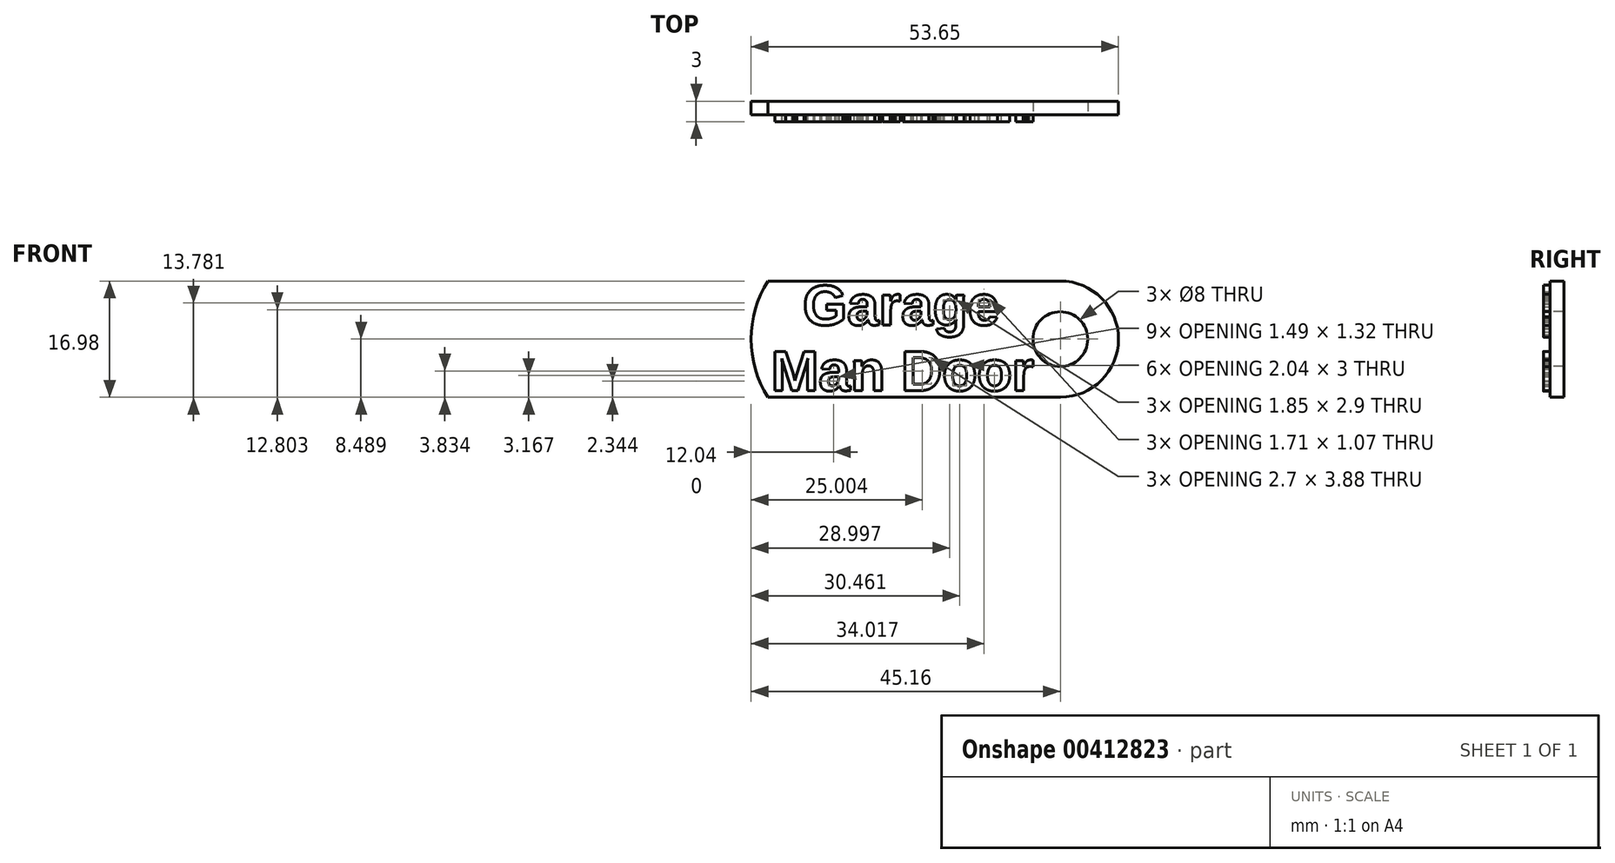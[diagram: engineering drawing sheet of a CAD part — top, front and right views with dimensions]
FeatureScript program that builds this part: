
annotation { "Feature Type Name" : "Feature", "Feature Type Description" : "" }
export const myFeature = defineFeature(function(context is Context, id is Id, definition is map)
    precondition{}
    {
        {
            var Q0;
            Q0=qCreatedBy(makeId("Front.planeOp"),FACE);
            var sketch = newSketch(context, id + "F0", { "sketchPlane" : qUnion([Q0])});
            skText(sketch, "E0", { "text": "   Garage \n Man Door\n", "fontName": "Arimo-Bold.ttf"});
            const initialGuessF0  = {"E0": [-0.02056, -3e-05, 1, 0, 0.006]};
            skSetInitialGuess(sketch, initialGuessF0);
            skSolve(sketch);
        }
        {
            var Q0;
            Q0=qSketchRegion(id+"F0",true);
            extrude(context, id + "F1", {"entities" : qUnion([Q0]), "depth" : 1 * mm});
        }
        {
            var Q0;
            Q0=qCreatedBy(makeId("Front.planeOp"),FACE);
            var sketch = newSketch(context, id + "F2", { "sketchPlane" : qUnion([Q0])});
            skCircle(sketch, "E1", {"center": v(24, -2.1) * mm, "radius": 4 * mm});
            skArc(sketch, "E2", {"start": v(24, -10.58) * mm, "mid": v(32.5, -2.1) * mm, "end": v(24, 6.4) * mm});
            skLineSegment(sketch, "E3", {"start": v(-18.72, 6.4) * mm, "end": v(24, 6.4) * mm});
            skLineSegment(sketch, "E4", {"start": v(-18.72, -10.58) * mm, "end": v(24, -10.58) * mm});
            skArc(sketch, "E5", {"start": v(-18.72, 6.4) * mm, "mid": v(-21.16, -2.1) * mm, "end": v(-18.72, -10.58) * mm});
            skSolve(sketch);
        }
        {
            var Q0;
            Q0=qSketchRegion(id+"F2",true);
            extrude(context, id + "F3", {"entities" : qUnion([Q0]), "oppositeDirection" : true, "depth" : 2 * mm});
        }
    });
